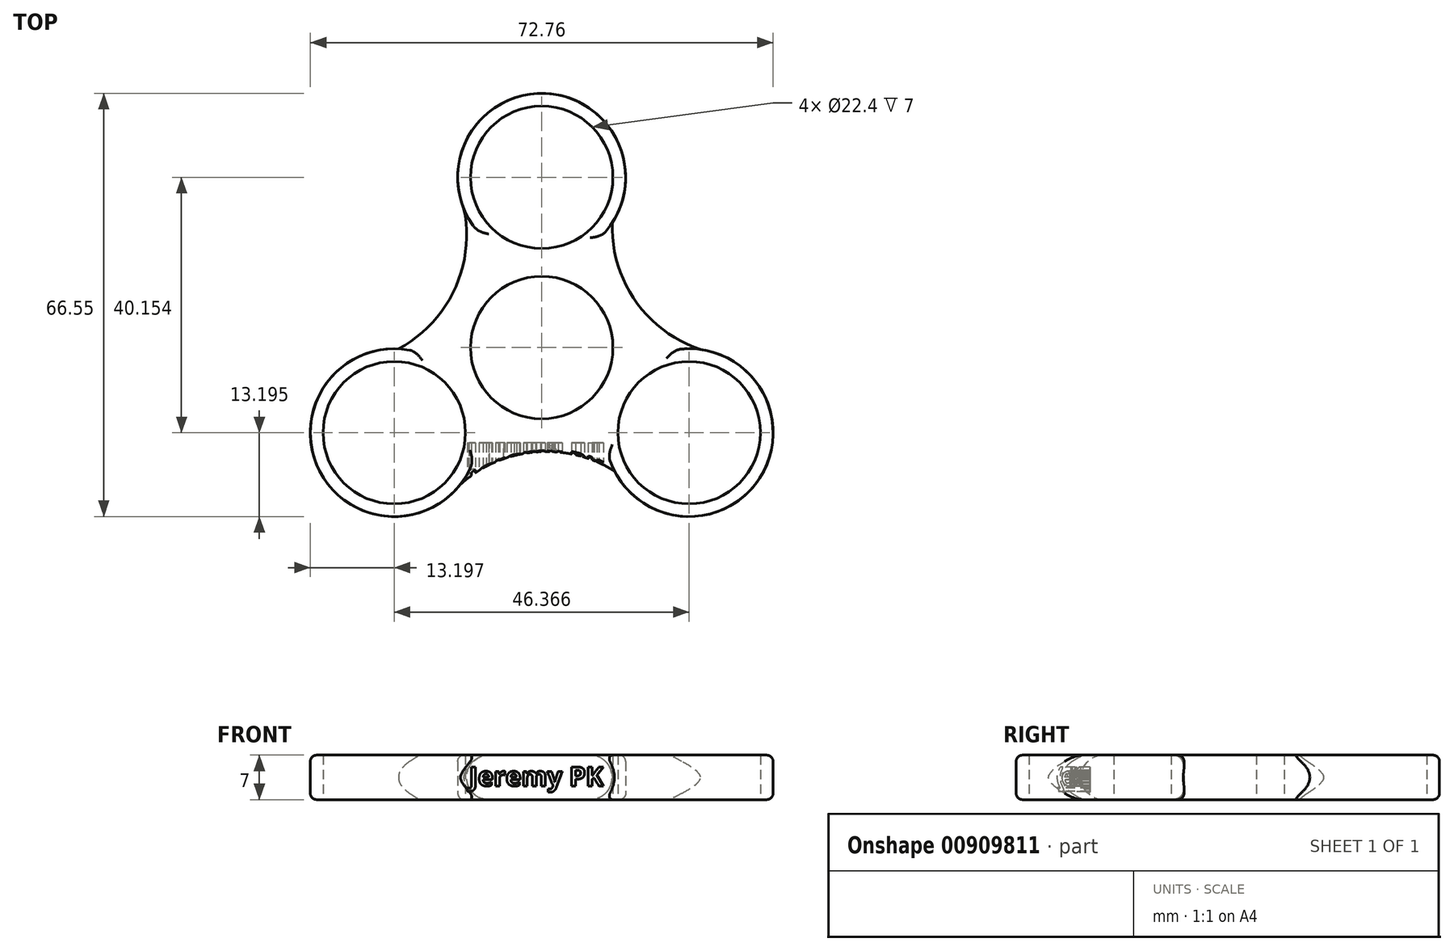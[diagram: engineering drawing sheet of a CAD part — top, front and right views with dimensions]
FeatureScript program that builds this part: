
annotation { "Feature Type Name" : "Feature", "Feature Type Description" : "" }
export const myFeature = defineFeature(function(context is Context, id is Id, definition is map)
    precondition{}
    {
        {
            var Q0;
            Q0=qCreatedBy(makeId("Top.planeOp"),FACE);
            var sketch = newSketch(context, id + "F0", { "sketchPlane" : qUnion([Q0])});
            skCircle(sketch, "E0", {"center": v(0, 0) * mm, "radius": 11.2 * mm});
            skCircle(sketch, "E1", {"center": v(0, 26.77) * mm, "radius": 11.2 * mm});
            skArc(sketch, "E2", {"start": v(11.08, 19.6) * mm, "mid": v(1.24, 39.91) * mm, "end": v(-12.23, 21.8) * mm});
            skCircle(sketch, "E3.1.0", {"center": v(-23.18, -13.38) * mm, "radius": 11.2 * mm});
            skArc(sketch, "E3.1.1", {"start": v(-22.52, -0.2) * mm, "mid": v(-35.18, -18.88) * mm, "end": v(-12.77, -21.5) * mm});
            skCircle(sketch, "E3.2.0", {"center": v(23.18, -13.38) * mm, "radius": 11.2 * mm});
            skArc(sketch, "E3.2.1", {"start": v(11.43, -19.4) * mm, "mid": v(33.94, -21.03) * mm, "end": v(25, -0.3) * mm});
            skLineSegment(sketch, "E4", {"start": v(-23.18, -13.38) * mm, "end": v(52.37, 30.36) * mm, "construction": true});
            skLineSegment(sketch, "E5", {"start": v(23.18, -13.38) * mm, "end": v(-46.69, 27.52) * mm, "construction": true});
            skLineSegment(sketch, "E6", {"start": v(23.18, -13.38) * mm, "end": v(0, 26.77) * mm, "construction": true});
            skArc(sketch, "E7", {"start": v(11.08, 19.6) * mm, "mid": v(14.74, 7.34) * mm, "end": v(25, -0.3) * mm});
            skArc(sketch, "E8.1.0", {"start": v(-22.52, -0.2) * mm, "mid": v(-13.73, 9.1) * mm, "end": v(-12.23, 21.8) * mm});
            skArc(sketch, "E8.2.0", {"start": v(11.43, -19.4) * mm, "mid": v(-1.01, -16.43) * mm, "end": v(-12.77, -21.5) * mm});
            skSolve(sketch);
        }
        {
            var Q0;
            Q0=makeQuery(id+"F0.imprint","IMPRINT",FACE,{"disambiguationData":[TD([[makeQuery(id+"F0.imprint","IMPRINT",EDGE,{"derivedFrom":sQuery(id+"F0.wireOp",EDGE,"E0")}),-1.0]])]});
            extrude(context, id + "F1", {"entities" : qUnion([Q0]), "depth" : 7 * mm, "offsetDistance" : 25 * mm});
        }
        {
            var Q0;
            Q0=makeQuery(id+"F1.opExtrude","CAP_EDGE",EDGE,{"disambiguationData":[OSD([sQuery(id+"F0.wireOp",EDGE,"E7")])],"isStart":false});
            var Q1;
            Q1=makeQuery(id+"F1.opExtrude","CAP_EDGE",EDGE,{"disambiguationData":[OSD([sQuery(id+"F0.wireOp",EDGE,"E7")])],"isStart":true});
            var Q2;
            Q2=makeQuery(id+"F1.opExtrude","CAP_EDGE",EDGE,{"disambiguationData":[OSD([sQuery(id+"F0.wireOp",EDGE,"E8.1.0")])],"isStart":false});
            var Q3;
            Q3=makeQuery(id+"F1.opExtrude","CAP_EDGE",EDGE,{"disambiguationData":[OSD([sQuery(id+"F0.wireOp",EDGE,"E8.1.0")])],"isStart":true});
            var Q4;
            Q4=makeQuery(id+"F1.opExtrude","CAP_EDGE",EDGE,{"disambiguationData":[OSD([sQuery(id+"F0.wireOp",EDGE,"E8.2.0")])],"isStart":false});
            var Q5;
            Q5=makeQuery(id+"F1.opExtrude","CAP_EDGE",EDGE,{"disambiguationData":[OSD([sQuery(id+"F0.wireOp",EDGE,"E8.2.0")])],"isStart":true});
            fillet(context, id + "F2", {"entities" : qUnion([Q0, Q1, Q2, Q3, Q4, Q5]), "radius" : 3.5 * mm, "tangentPropagation" : true, "allowEdgeOverflow" : false});
        }
        {
            var Q0;
            Q0=makeQuery(id+"F1.opExtrude","CAP_EDGE",EDGE,{"disambiguationData":[OSD([sQuery(id+"F0.wireOp",EDGE,"E2")])],"isStart":true});
            var Q1;
            Q1=makeQuery(id+"F1.opExtrude","CAP_EDGE",EDGE,{"disambiguationData":[OSD([sQuery(id+"F0.wireOp",EDGE,"E2")])],"isStart":false});
            var Q2;
            Q2=makeQuery(id+"F1.opExtrude","CAP_EDGE",EDGE,{"disambiguationData":[OSD([sQuery(id+"F0.wireOp",EDGE,"E3.1.1")])],"isStart":true});
            var Q3;
            Q3=makeQuery(id+"F1.opExtrude","CAP_EDGE",EDGE,{"disambiguationData":[OSD([sQuery(id+"F0.wireOp",EDGE,"E3.1.1")])],"isStart":false});
            var Q4;
            Q4=makeQuery(id+"F1.opExtrude","CAP_EDGE",EDGE,{"disambiguationData":[OSD([sQuery(id+"F0.wireOp",EDGE,"E3.2.1")])],"isStart":true});
            var Q5;
            Q5=makeQuery(id+"F1.opExtrude","CAP_EDGE",EDGE,{"disambiguationData":[OSD([sQuery(id+"F0.wireOp",EDGE,"E3.2.1")])],"isStart":false});
            fillet(context, id + "F3", {"entities" : qUnion([Q0, Q1, Q2, Q3, Q4, Q5]), "radius" : 1 * mm, "tangentPropagation" : true, "allowEdgeOverflow" : false});
        }
        {
            var Q0;
            Q0=qCreatedBy(makeId("Front.planeOp"),FACE);
            cPlane(context, id + "F4", {"entities" : qUnion([Q0]), "cplaneType" : CPlaneType.OFFSET, "offset" : 49.4 * mm, "width" : 150 * mm, "height" : 150 * mm});
        }
        {
            var Q0;
            Q0=qCreatedBy(id+"F4.planeOp",FACE);
            var sketch = newSketch(context, id + "F5", { "sketchPlane" : qUnion([Q0])});
            skText(sketch, "E9", { "text": "Jeremy PK", "fontName": "OpenSans-Bold.ttf"});
            const initialGuessF5  = {"E9": [-0.01141, 0.00216, 1, 0, 0.003]};
            skSetInitialGuess(sketch, initialGuessF5);
            skSolve(sketch);
        }
        {
            var Q0;
            Q0 = qSketchRegion(id + "F5", true);
            extrude(context, id + "F6", {"entities" : qUnion([Q0]), "operationType" : NewBodyOperationType.REMOVE, "oppositeDirection" : true, "depth" : 34.4 * mm, "offsetDistance" : 25 * mm});
        }
    });
